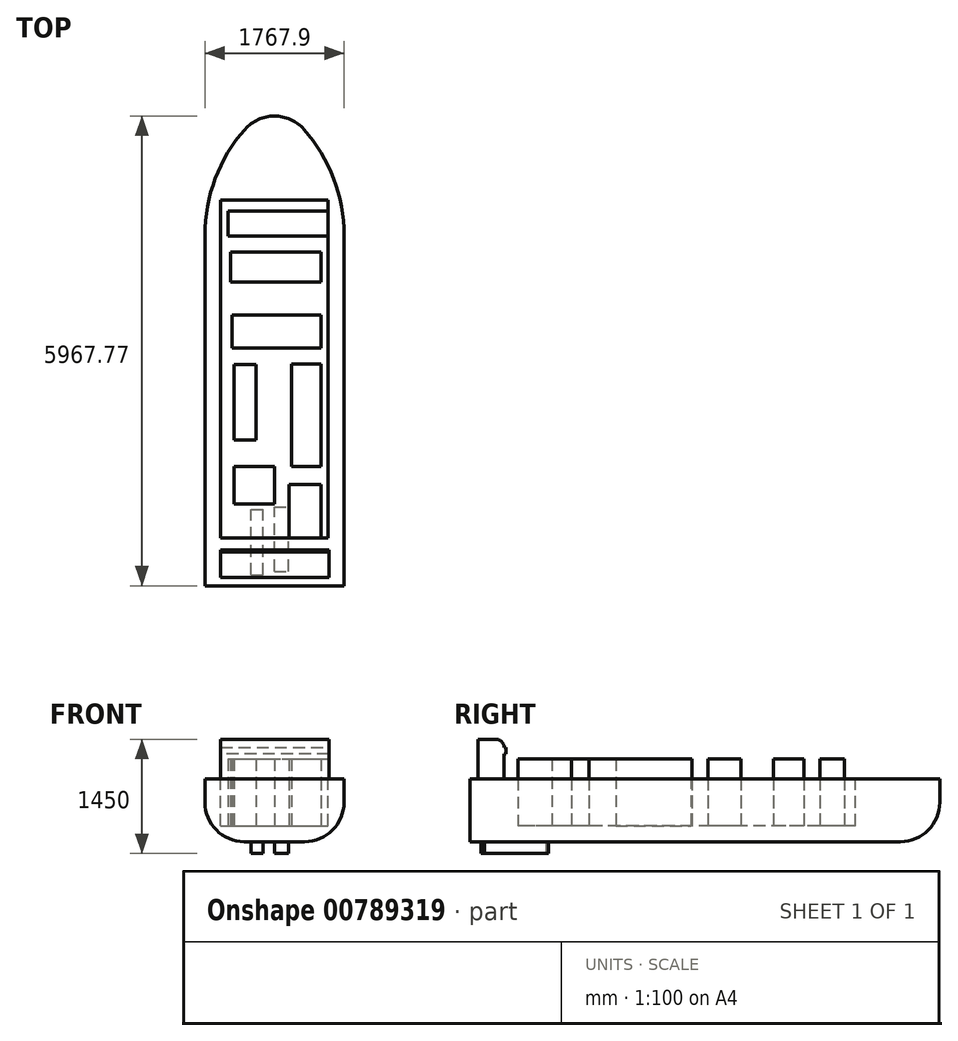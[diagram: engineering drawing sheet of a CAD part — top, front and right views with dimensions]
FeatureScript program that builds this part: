
annotation { "Feature Type Name" : "Feature", "Feature Type Description" : "" }
export const myFeature = defineFeature(function(context is Context, id is Id, definition is map)
    precondition{}
    {
        {
            var Q0;
            Q0=qCreatedBy(makeId("Top.planeOp"),FACE);
            var sketch = newSketch(context, id + "F0", { "sketchPlane" : qUnion([Q0])});
            skLineSegment(sketch, "E0.bottom", {"start": v(-883.95, 1738.93) * mm, "end": v(883.95, 1738.93) * mm});
            skLineSegment(sketch, "E0.top", {"start": v(-883.95, -2714.44) * mm, "end": v(883.95, -2714.44) * mm});
            skLineSegment(sketch, "E0.left", {"start": v(-883.95, 1738.93) * mm, "end": v(-883.95, -2714.44) * mm});
            skLineSegment(sketch, "E0.right", {"start": v(883.95, 1738.93) * mm, "end": v(883.95, -2714.44) * mm});
            skArc(sketch, "E1", {"start": v(0, 3415.53) * mm, "mid": v(-649.43, 2686.6) * mm, "end": v(-883.95, 1738.93) * mm});
            skArc(sketch, "E2", {"start": v(883.95, 1738.93) * mm, "mid": v(649.43, 2686.6) * mm, "end": v(0, 3415.53) * mm});
            skSolve(sketch);
        }
        {
            var Q0;
            Q0=makeQuery(id+"F0.imprint","IMPRINT",FACE,{"disambiguationData":[TD([[makeQuery(id+"F0.imprint","IMPRINT",EDGE,{"derivedFrom":sQuery(id+"F0.wireOp",EDGE,"E0.bottom")}),1.0]])]});
            var Q1;
            Q1=makeQuery(id+"F0.imprint","IMPRINT",FACE,{"disambiguationData":[TD([[makeQuery(id+"F0.imprint","IMPRINT",EDGE,{"derivedFrom":sQuery(id+"F0.wireOp",EDGE,"E0.bottom")}),-1.0]])]});
            extrude(context, id + "F1", {"entities" : qUnion([Q0, Q1]), "depth" : 800 * mm, "offsetDistance" : 25 * mm});
        }
        {
            var Q0;
            Q0=makeQuery(id+"F1.opExtrude","CAP_EDGE",EDGE,{"disambiguationData":[OSD([sQuery(id+"F0.wireOp",EDGE,"E0.left")])],"isStart":true});
            fillet(context, id + "F2", {"entities" : qUnion([Q0]), "radius" : 500 * mm, "tangentPropagation" : true, "allowEdgeOverflow" : false});
        }
        {
            var Q0;
            Q0=makeQuery(id+"F1.opExtrude","CAP_EDGE",EDGE,{"disambiguationData":[OSD([sQuery(id+"F0.wireOp",EDGE,"E0.right")])],"isStart":true});
            fillet(context, id + "F3", {"entities" : qUnion([Q0]), "radius" : 500 * mm, "tangentPropagation" : true, "allowEdgeOverflow" : false});
        }
        {
            var Q0;
            Q0=makeQuery(id+"F1.opExtrude","CAP_FACE",FACE,{"disambiguationData":[OSD([sQuery(id+"F0.wireOp",EDGE,"E0.top"),sQuery(id+"F0.wireOp",EDGE,"E0.left"),sQuery(id+"F0.wireOp",EDGE,"E0.right"),sQuery(id+"F0.wireOp",EDGE,"E1"),sQuery(id+"F0.wireOp",EDGE,"E2")])],"isStart":false});
            var sketch = newSketch(context, id + "F4", { "sketchPlane" : qUnion([Q0])});
            skLineSegment(sketch, "E3.bottom", {"start": v(-683.95, 2183.41) * mm, "end": v(683.95, 2183.41) * mm});
            skLineSegment(sketch, "E3.top", {"start": v(-683.95, -2107.7) * mm, "end": v(683.95, -2107.7) * mm});
            skLineSegment(sketch, "E3.left", {"start": v(-683.95, 2183.41) * mm, "end": v(-683.95, -2107.7) * mm});
            skLineSegment(sketch, "E3.right", {"start": v(683.95, 2183.41) * mm, "end": v(683.95, -2107.7) * mm});
            skSolve(sketch);
        }
        {
            var Q0;
            Q0=makeQuery(id+"F4.imprint","IMPRINT",FACE,{"disambiguationData":[TD([[makeQuery(id+"F4.imprint","IMPRINT",EDGE,{"derivedFrom":sQuery(id+"F4.wireOp",EDGE,"E3.bottom")}),-1.0]])]});
            extrude(context, id + "F5", {"entities" : qUnion([Q0]), "operationType" : NewBodyOperationType.REMOVE, "oppositeDirection" : true, "depth" : 600 * mm, "offsetDistance" : 25 * mm});
        }
        {
            var Q0;
            Q0=makeQuery(id+"F1.opExtrude","CAP_FACE",FACE,{"disambiguationData":[OSD([sQuery(id+"F0.wireOp",EDGE,"E0.top"),sQuery(id+"F0.wireOp",EDGE,"E0.left"),sQuery(id+"F0.wireOp",EDGE,"E0.right"),sQuery(id+"F0.wireOp",EDGE,"E1"),sQuery(id+"F0.wireOp",EDGE,"E2")])],"isStart":false});
            var sketch = newSketch(context, id + "F6", { "sketchPlane" : qUnion([Q0])});
            skLineSegment(sketch, "E4.bottom", {"start": v(-683.95, -2283.22) * mm, "end": v(693.1, -2283.22) * mm});
            skLineSegment(sketch, "E4.top", {"start": v(-683.95, -2610.06) * mm, "end": v(693.1, -2610.06) * mm});
            skLineSegment(sketch, "E4.left", {"start": v(-683.95, -2283.22) * mm, "end": v(-683.95, -2610.06) * mm});
            skLineSegment(sketch, "E4.right", {"start": v(693.1, -2283.22) * mm, "end": v(693.1, -2610.06) * mm});
            skSolve(sketch);
        }
        {
            var Q0;
            Q0=makeQuery(id+"F6.imprint","IMPRINT",FACE,{"disambiguationData":[TD([[makeQuery(id+"F6.imprint","IMPRINT",EDGE,{"derivedFrom":sQuery(id+"F6.wireOp",EDGE,"E4.bottom")}),-1.0]])]});
            extrude(context, id + "F7", {"entities" : qUnion([Q0]), "operationType" : NewBodyOperationType.ADD, "depth" : 500 * mm, "offsetDistance" : 25 * mm});
        }
        {
            var Q0;
            Q0=makeQuery(id+"F7.opExtrude","CAP_EDGE",EDGE,{"disambiguationData":[OSD([sQuery(id+"F6.wireOp",EDGE,"E4.bottom")])],"isStart":false});
            fillet(context, id + "F8", {"entities" : qUnion([Q0]), "radius" : 100 * mm, "tangentPropagation" : true, "allowEdgeOverflow" : false});
        }
        {
            var Q0;
            Q0=makeQuery(id+"F7.opExtrude","SWEPT_FACE",FACE,{"disambiguationData":[OSD([sQuery(id+"F6.wireOp",EDGE,"E4.bottom")])]});
            var sketch = newSketch(context, id + "F9", { "sketchPlane" : qUnion([Q0])});
            skLineSegment(sketch, "E5.bottom", {"start": v(-693.1, 1200) * mm, "end": v(683.95, 1200) * mm});
            skLineSegment(sketch, "E5.top", {"start": v(-693.1, 1114.25) * mm, "end": v(683.95, 1114.25) * mm});
            skLineSegment(sketch, "E5.left", {"start": v(-693.1, 1200) * mm, "end": v(-693.1, 1114.25) * mm});
            skLineSegment(sketch, "E5.right", {"start": v(683.95, 1200) * mm, "end": v(683.95, 1114.25) * mm});
            skSolve(sketch);
        }
        {
            var Q0;
            Q0=makeQuery(id+"F9.imprint","IMPRINT",FACE,{"disambiguationData":[TD([[makeQuery(id+"F9.imprint","IMPRINT",EDGE,{"derivedFrom":sQuery(id+"F9.wireOp",EDGE,"E5.bottom")}),1.0]])]});
            extrude(context, id + "F10", {"entities" : qUnion([Q0]), "operationType" : NewBodyOperationType.ADD, "depth" : 25 * mm, "offsetDistance" : 25 * mm});
        }
        {
            var Q0;
            Q0=makeQuery(id+"F5.boolean.opBoolean","COPY",FACE,{"derivedFrom":makeQuery(id+"F5.opExtrude","CAP_FACE",FACE,{"disambiguationData":[OSD([sQuery(id+"F4.wireOp",EDGE,"E3.bottom"),sQuery(id+"F4.wireOp",EDGE,"E3.top"),sQuery(id+"F4.wireOp",EDGE,"E3.left"),sQuery(id+"F4.wireOp",EDGE,"E3.right")])],"isStart":false})});
            var sketch = newSketch(context, id + "F11", { "sketchPlane" : qUnion([Q0])});
            skLineSegment(sketch, "E6.bottom", {"start": v(-591.68, 2044.48) * mm, "end": v(683.95, 2044.48) * mm});
            skLineSegment(sketch, "E6.top", {"start": v(-591.68, 1728.92) * mm, "end": v(683.95, 1728.92) * mm});
            skLineSegment(sketch, "E6.left", {"start": v(-591.68, 2044.48) * mm, "end": v(-591.68, 1728.92) * mm});
            skLineSegment(sketch, "E6.right", {"start": v(683.95, 2044.48) * mm, "end": v(683.95, 1728.92) * mm});
            skLineSegment(sketch, "E7.bottom", {"start": v(-557.87, 1526.06) * mm, "end": v(591.68, 1526.06) * mm});
            skLineSegment(sketch, "E7.top", {"start": v(-557.87, 1142.87) * mm, "end": v(591.68, 1142.87) * mm});
            skLineSegment(sketch, "E7.left", {"start": v(-557.87, 1526.06) * mm, "end": v(-557.87, 1142.87) * mm});
            skLineSegment(sketch, "E7.right", {"start": v(591.68, 1526.06) * mm, "end": v(591.68, 1142.87) * mm});
            skLineSegment(sketch, "E8.bottom", {"start": v(-535.33, 725.88) * mm, "end": v(591.68, 725.88) * mm});
            skLineSegment(sketch, "E8.top", {"start": v(-535.33, 308.9) * mm, "end": v(591.68, 308.9) * mm});
            skLineSegment(sketch, "E8.left", {"start": v(-535.33, 725.88) * mm, "end": v(-535.33, 308.9) * mm});
            skLineSegment(sketch, "E8.right", {"start": v(591.68, 725.88) * mm, "end": v(591.68, 308.9) * mm});
            skLineSegment(sketch, "E9.bottom", {"start": v(-512.79, -863.2) * mm, "end": v(-231.04, -863.2) * mm});
            skLineSegment(sketch, "E9.top", {"start": v(-512.79, 94.76) * mm, "end": v(-231.04, 94.76) * mm});
            skLineSegment(sketch, "E9.left", {"start": v(-512.79, -863.2) * mm, "end": v(-512.79, 94.76) * mm});
            skLineSegment(sketch, "E9.right", {"start": v(-231.04, -863.2) * mm, "end": v(-231.04, 94.76) * mm});
            skLineSegment(sketch, "E10.bottom", {"start": v(219.77, 106.03) * mm, "end": v(591.68, 106.03) * mm});
            skLineSegment(sketch, "E10.top", {"start": v(219.77, -1201.3) * mm, "end": v(591.68, -1201.3) * mm});
            skLineSegment(sketch, "E10.left", {"start": v(219.77, 106.03) * mm, "end": v(219.77, -1201.3) * mm});
            skLineSegment(sketch, "E10.right", {"start": v(591.68, 106.03) * mm, "end": v(591.68, -1201.3) * mm});
            skLineSegment(sketch, "E11.bottom", {"start": v(-512.79, -1201.3) * mm, "end": v(0, -1201.3) * mm});
            skLineSegment(sketch, "E11.top", {"start": v(-512.79, -1674.64) * mm, "end": v(0, -1674.64) * mm});
            skLineSegment(sketch, "E11.left", {"start": v(-512.79, -1201.3) * mm, "end": v(-512.79, -1674.64) * mm});
            skLineSegment(sketch, "E11.right", {"start": v(0, -1201.3) * mm, "end": v(0, -1674.64) * mm});
            skLineSegment(sketch, "E12.bottom", {"start": v(185.96, -1426.7) * mm, "end": v(591.68, -1426.7) * mm});
            skLineSegment(sketch, "E12.top", {"start": v(185.96, -2107.7) * mm, "end": v(591.68, -2107.7) * mm});
            skLineSegment(sketch, "E12.left", {"start": v(185.96, -1426.7) * mm, "end": v(185.96, -2107.7) * mm});
            skLineSegment(sketch, "E12.right", {"start": v(591.68, -1426.7) * mm, "end": v(591.68, -2107.7) * mm});
            skSolve(sketch);
        }
        {
            var Q0;
            Q0=makeQuery(id+"F11.imprint","IMPRINT",FACE,{"disambiguationData":[TD([[makeQuery(id+"F11.imprint","IMPRINT",EDGE,{"derivedFrom":sQuery(id+"F11.wireOp",EDGE,"E6.bottom")}),-1.0]])]});
            var Q1;
            Q1=makeQuery(id+"F11.imprint","IMPRINT",FACE,{"disambiguationData":[TD([[makeQuery(id+"F11.imprint","IMPRINT",EDGE,{"derivedFrom":sQuery(id+"F11.wireOp",EDGE,"E7.bottom")}),-1.0]])]});
            var Q2;
            Q2=makeQuery(id+"F11.imprint","IMPRINT",FACE,{"disambiguationData":[TD([[makeQuery(id+"F11.imprint","IMPRINT",EDGE,{"derivedFrom":sQuery(id+"F11.wireOp",EDGE,"E8.bottom")}),-1.0]])]});
            var Q3;
            Q3=makeQuery(id+"F11.imprint","IMPRINT",FACE,{"disambiguationData":[TD([[makeQuery(id+"F11.imprint","IMPRINT",EDGE,{"derivedFrom":sQuery(id+"F11.wireOp",EDGE,"E9.bottom")}),1.0]])]});
            var Q4;
            Q4=makeQuery(id+"F11.imprint","IMPRINT",FACE,{"disambiguationData":[TD([[makeQuery(id+"F11.imprint","IMPRINT",EDGE,{"derivedFrom":sQuery(id+"F11.wireOp",EDGE,"E10.bottom")}),-1.0]])]});
            var Q5;
            Q5=makeQuery(id+"F11.imprint","IMPRINT",FACE,{"disambiguationData":[TD([[makeQuery(id+"F11.imprint","IMPRINT",EDGE,{"derivedFrom":sQuery(id+"F11.wireOp",EDGE,"E11.bottom")}),-1.0]])]});
            var Q6;
            Q6=makeQuery(id+"F11.imprint","IMPRINT",FACE,{"disambiguationData":[TD([[makeQuery(id+"F11.imprint","IMPRINT",EDGE,{"derivedFrom":sQuery(id+"F11.wireOp",EDGE,"E12.bottom")}),-1.0]])]});
            extrude(context, id + "F12", {"entities" : qUnion([Q0, Q1, Q2, Q3, Q4, Q5, Q6]), "operationType" : NewBodyOperationType.ADD, "depth" : 850 * mm, "offsetDistance" : 25 * mm});
        }
        {
            var Q0;
            Q0=makeQuery(id+"F1.opExtrude","CAP_FACE",FACE,{"disambiguationData":[OSD([sQuery(id+"F0.wireOp",EDGE,"E0.top"),sQuery(id+"F0.wireOp",EDGE,"E0.left"),sQuery(id+"F0.wireOp",EDGE,"E0.right"),sQuery(id+"F0.wireOp",EDGE,"E1"),sQuery(id+"F0.wireOp",EDGE,"E2")])],"isStart":true});
            var sketch = newSketch(context, id + "F13", { "sketchPlane" : qUnion([Q0])});
            skLineSegment(sketch, "E13.bottom", {"start": v(-295.4, 2575.45) * mm, "end": v(-145.67, 2575.45) * mm});
            skLineSegment(sketch, "E13.top", {"start": v(-295.4, 1745.12) * mm, "end": v(-145.67, 1745.12) * mm});
            skLineSegment(sketch, "E13.left", {"start": v(-295.4, 2575.45) * mm, "end": v(-295.4, 1745.12) * mm});
            skLineSegment(sketch, "E13.right", {"start": v(-145.67, 2575.45) * mm, "end": v(-145.67, 1745.12) * mm});
            skLineSegment(sketch, "E14.bottom", {"start": v(0, 2529.59) * mm, "end": v(179.68, 2529.59) * mm});
            skLineSegment(sketch, "E14.top", {"start": v(0, 1715.47) * mm, "end": v(179.68, 1715.47) * mm});
            skLineSegment(sketch, "E14.left", {"start": v(0, 2529.59) * mm, "end": v(0, 1715.47) * mm});
            skLineSegment(sketch, "E14.right", {"start": v(179.68, 2529.59) * mm, "end": v(179.68, 1715.47) * mm});
            skSolve(sketch);
        }
        {
            var Q0;
            Q0=makeQuery(id+"F13.imprint","IMPRINT",FACE,{"disambiguationData":[TD([[makeQuery(id+"F13.imprint","IMPRINT",EDGE,{"derivedFrom":sQuery(id+"F13.wireOp",EDGE,"E13.bottom")}),-1.0]])]});
            var Q1;
            Q1=makeQuery(id+"F13.imprint","IMPRINT",FACE,{"disambiguationData":[TD([[makeQuery(id+"F13.imprint","IMPRINT",EDGE,{"derivedFrom":sQuery(id+"F13.wireOp",EDGE,"E14.bottom")}),-1.0]])]});
            extrude(context, id + "F14", {"entities" : qUnion([Q0, Q1]), "operationType" : NewBodyOperationType.ADD, "oppositeDirection" : true, "depth" : -150 * mm, "offsetDistance" : 25 * mm});
        }
    });
